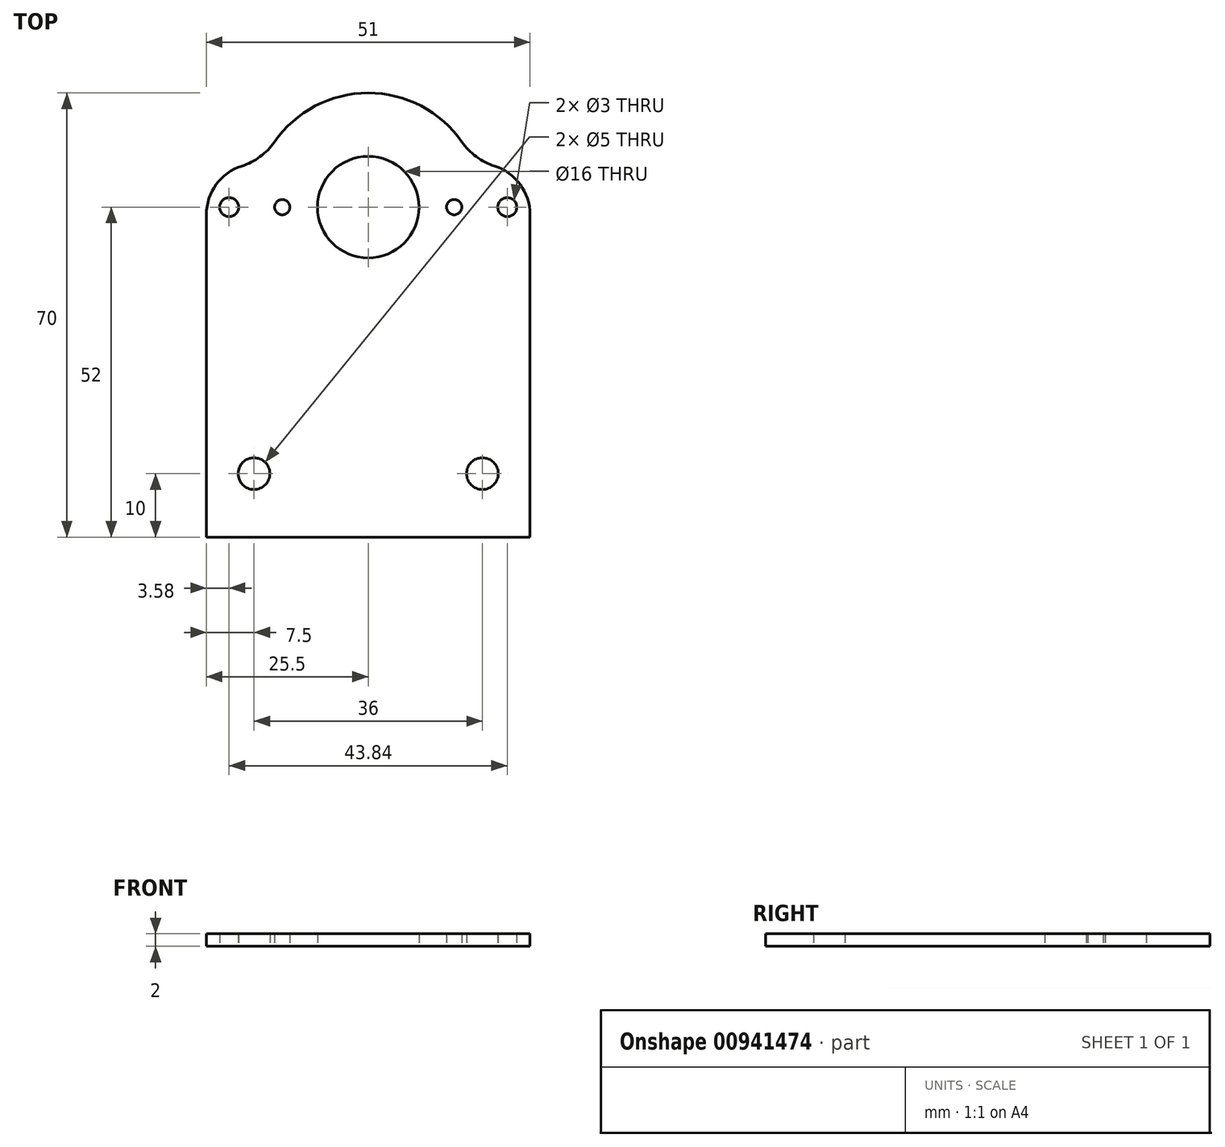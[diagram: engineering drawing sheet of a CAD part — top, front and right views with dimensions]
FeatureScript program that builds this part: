
annotation { "Feature Type Name" : "Feature", "Feature Type Description" : "" }
export const myFeature = defineFeature(function(context is Context, id is Id, definition is map)
    precondition{}
    {
        {
            var Q0;
            Q0=qCreatedBy(makeId("Top.planeOp"),FACE);
            var sketch = newSketch(context, id + "F0", { "sketchPlane" : qUnion([Q0])});
            skCircle(sketch, "E0", {"center": v(0, 0) * mm, "radius": 8 * mm});
            skCircle(sketch, "E1", {"center": v(0, 0) * mm, "radius": 18 * mm});
            skLineSegment(sketch, "E2.bottom", {"start": v(25.5, -52) * mm, "end": v(-25.5, -52) * mm});
            skLineSegment(sketch, "E2.top", {"start": v(25.5, 6) * mm, "end": v(-25.5, 6) * mm});
            skLineSegment(sketch, "E2.left", {"start": v(25.5, -52) * mm, "end": v(25.5, 6) * mm});
            skLineSegment(sketch, "E2.right", {"start": v(-25.5, -52) * mm, "end": v(-25.5, 6) * mm});
            skPoint(sketch, "E2.middle", {"position": v(0, -23) * mm});
            skCircle(sketch, "E3", {"center": v(-21.92, 0) * mm, "radius": 1.5 * mm});
            skCircle(sketch, "E4", {"center": v(21.92, 0) * mm, "radius": 1.5 * mm});
            skCircle(sketch, "E5", {"center": v(-13.55, 0) * mm, "radius": 1.2 * mm});
            skCircle(sketch, "E6", {"center": v(13.55, 0) * mm, "radius": 1.2 * mm});
            skCircle(sketch, "E7", {"center": v(-18, -42) * mm, "radius": 2.5 * mm});
            skCircle(sketch, "E8", {"center": v(18, -42) * mm, "radius": 2.5 * mm});
            skSolve(sketch);
        }
        {
            var Q0;
            {var subQ0=sQuery(id+"F0.wireOp",EDGE,"E2.top");var subQ1=sQuery(id+"F0.wireOp",EDGE,"E1");var subQ2=makeQuery(id+"F0.imprint","INTERSECT",VERTEX,{"disambiguationData":[OD(0.0)],"derivedFrom":[subQ1,subQ0]});Q0=makeQuery(id+"F0.imprint","IMPRINT",FACE,{"disambiguationData":[TD([[makeQuery(id+"F0.imprint","IMPRINT",EDGE,{"disambiguationData":[TD([[subQ2,-1.0]])],"derivedFrom":subQ1}),1.0]])]});}
            var Q1;
            Q1=makeQuery(id+"F0.imprint","IMPRINT",FACE,{"disambiguationData":[TD([[makeQuery(id+"F0.imprint","IMPRINT",EDGE,{"derivedFrom":sQuery(id+"F0.wireOp",EDGE,"E0")}),-1.0]])]});
            var Q2;
            Q2=makeQuery(id+"F0.imprint","IMPRINT",FACE,{"disambiguationData":[TD([[makeQuery(id+"F0.imprint","IMPRINT",EDGE,{"derivedFrom":sQuery(id+"F0.wireOp",EDGE,"E2.bottom")}),-1.0]])]});
            var Q3;
            Q3=makeQuery(id+"F0.imprint","IMPRINT",FACE,{"disambiguationData":[TD([[makeQuery(id+"F0.imprint","IMPRINT",EDGE,{"derivedFrom":sQuery(id+"F0.wireOp",EDGE,"E5")}),-1.0]])]});
            extrude(context, id + "F1", {"entities" : qUnion([Q0, Q1, Q2, Q3]), "depth" : 2 * mm, "offsetDistance" : 25 * mm});
        }
        {
            var Q0;
            {var subQ0=sQuery(id+"F0.wireOp",EDGE,"E2.top");var subQ1=sQuery(id+"F0.wireOp",EDGE,"E1");Q0=makeQuery(id+"F1.opExtrude","SWEPT_EDGE",EDGE,{"disambiguationData":[OSD([subQ1,subQ0]),TDD([makeQuery(id+"F0.imprint","INTERSECT",VERTEX,{"disambiguationData":[OD(1.0)],"derivedFrom":[subQ1,subQ0]})])]});}
            var Q1;
            {var subQ0=sQuery(id+"F0.wireOp",EDGE,"E2.top");var subQ1=sQuery(id+"F0.wireOp",EDGE,"E1");Q1=makeQuery(id+"F1.opExtrude","SWEPT_EDGE",EDGE,{"disambiguationData":[OSD([subQ1,subQ0]),TDD([makeQuery(id+"F0.imprint","INTERSECT",VERTEX,{"disambiguationData":[OD(0.0)],"derivedFrom":[subQ1,subQ0]})])]});}
            fillet(context, id + "F2", {"entities" : qUnion([Q0, Q1]), "tangentPropagation" : true, "radius" : 10 * mm, "defaultsChanged" : false, "vertexSettings" : [], "allowEdgeOverflow" : false});
        }
        {
            var Q0;
            Q0=makeQuery(id+"F1.opExtrude","SWEPT_EDGE",EDGE,{"disambiguationData":[OSD([sQuery(id+"F0.wireOp",EDGE,"E2.top"),sQuery(id+"F0.wireOp",EDGE,"E2.left")])]});
            var Q1;
            Q1=makeQuery(id+"F1.opExtrude","SWEPT_EDGE",EDGE,{"disambiguationData":[OSD([sQuery(id+"F0.wireOp",EDGE,"E2.top"),sQuery(id+"F0.wireOp",EDGE,"E2.right")])]});
            fillet(context, id + "F3", {"entities" : qUnion([Q0, Q1]), "tangentPropagation" : true, "radius" : 8 * mm, "defaultsChanged" : true, "vertexSettings" : [], "allowEdgeOverflow" : false});
        }
    });
